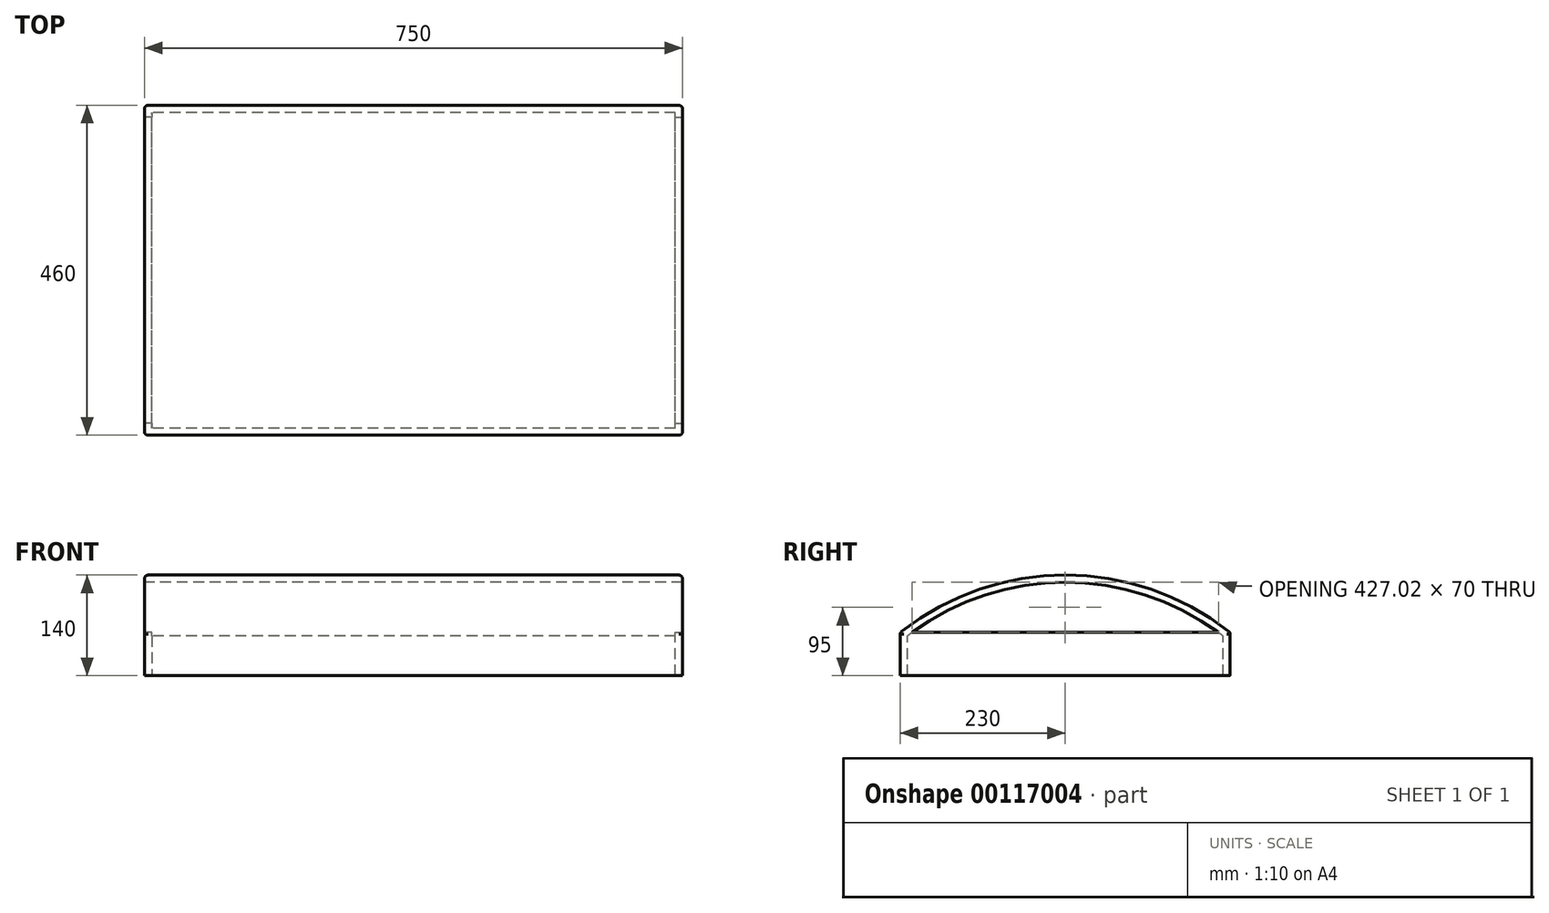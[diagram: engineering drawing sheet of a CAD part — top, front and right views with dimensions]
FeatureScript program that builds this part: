
annotation { "Feature Type Name" : "Feature", "Feature Type Description" : "" }
export const myFeature = defineFeature(function(context is Context, id is Id, definition is map)
    precondition{}
    {
        {
            var Q0;
            Q0=qCreatedBy(makeId("Right.planeOp"),FACE);
            var sketch = newSketch(context, id + "F0", { "sketchPlane" : qUnion([Q0])});
            skLineSegment(sketch, "E0.bottom", {"start": v(-230, 30) * mm, "end": v(230, 30) * mm});
            skLineSegment(sketch, "E0.top", {"start": v(-230, -30) * mm, "end": v(230, -30) * mm});
            skLineSegment(sketch, "E0.left", {"start": v(-230, 30) * mm, "end": v(-230, -30) * mm});
            skLineSegment(sketch, "E0.right", {"start": v(230, 30) * mm, "end": v(230, -30) * mm});
            skPoint(sketch, "E0.middle", {"position": v(0, 0) * mm});
            skPoint(sketch, "E1", {"position": v(0, 110) * mm});
            skFitSpline(sketch, "E2", {"points": [v(-230, 30) * mm, v(230, 30) * mm], "startDerivative": vector(460, 0) * mm, "endDerivative": vector(460, 0) * mm});
            skArc(sketch, "E3", {"start": v(230, 30) * mm, "mid": v(0, 110) * mm, "end": v(-230, 30) * mm});
            skArc(sketch, "E4.0", {"start": v(220, 25.12) * mm, "mid": v(0, 100) * mm, "end": v(-220, 25.12) * mm});
            skLineSegment(sketch, "E5.0", {"start": v(-220, 25.12) * mm, "end": v(-220, -30) * mm});
            skLineSegment(sketch, "E6.0", {"start": v(220, 25.12) * mm, "end": v(220, -30) * mm});
            skSolve(sketch);
        }
        {
            var Q0;
            {var subQ4=sQuery(id+"F0.wireOp",EDGE,"E0.left");Q0=makeQuery(id+"F0.imprint","IMPRINT",FACE,{"disambiguationData":[TD([[makeQuery(id+"F0.imprint","IMPRINT",EDGE,{"derivedFrom":subQ4}),1.0]])]});}
            var Q1;
            {var subQ0=sQuery(id+"F0.wireOp",EDGE,"E3");Q1=makeQuery(id+"F0.imprint","IMPRINT",FACE,{"disambiguationData":[TD([[makeQuery(id+"F0.imprint","IMPRINT",EDGE,{"derivedFrom":subQ0}),1.0]])]});}
            var Q2;
            {var subQ4=sQuery(id+"F0.wireOp",EDGE,"E0.right");Q2=makeQuery(id+"F0.imprint","IMPRINT",FACE,{"disambiguationData":[TD([[makeQuery(id+"F0.imprint","IMPRINT",EDGE,{"derivedFrom":subQ4}),-1.0]])]});}
            extrude(context, id + "F1", {"entities" : qUnion([Q0, Q1, Q2]), "depth" : 750 * mm});
        }
        {
            var Q0;
            {var subQ0=sQuery(id+"F0.wireOp",EDGE,"E3");Q0=makeQuery(id+"F0.imprint","IMPRINT",FACE,{"disambiguationData":[TD([[makeQuery(id+"F0.imprint","IMPRINT",EDGE,{"derivedFrom":subQ0}),1.0]])]});}
            var Q1;
            {var subQ4=sQuery(id+"F0.wireOp",EDGE,"E0.left");Q1=makeQuery(id+"F0.imprint","IMPRINT",FACE,{"disambiguationData":[TD([[makeQuery(id+"F0.imprint","IMPRINT",EDGE,{"derivedFrom":subQ4}),1.0]])]});}
            var Q2;
            {var subQ0=sQuery(id+"F0.wireOp",EDGE,"E5.0");Q2=makeQuery(id+"F0.imprint","IMPRINT",FACE,{"disambiguationData":[TD([[makeQuery(id+"F0.imprint","IMPRINT",EDGE,{"derivedFrom":subQ0}),1.0]])]});}
            var Q3;
            {var subQ0=sQuery(id+"F0.wireOp",EDGE,"E4.0");var subQ1=sQuery(id+"F0.wireOp",EDGE,"E2");var subQ2=makeQuery(id+"F0.imprint","INTERSECT",VERTEX,{"disambiguationData":[OD(0.0)],"derivedFrom":[subQ1,subQ0]});Q3=makeQuery(id+"F0.imprint","IMPRINT",FACE,{"disambiguationData":[TD([[makeQuery(id+"F0.imprint","IMPRINT",EDGE,{"disambiguationData":[TD([[subQ2,-1.0]])],"derivedFrom":subQ1}),1.0]])]});}
            var Q4;
            {var subQ4=sQuery(id+"F0.wireOp",EDGE,"E0.right");Q4=makeQuery(id+"F0.imprint","IMPRINT",FACE,{"disambiguationData":[TD([[makeQuery(id+"F0.imprint","IMPRINT",EDGE,{"derivedFrom":subQ4}),-1.0]])]});}
            extrude(context, id + "F2", {"entities" : qUnion([Q0, Q1, Q2, Q3, Q4]), "depth" : 10 * mm});
        }
        {
            var Q0;
            Q0=qCreatedBy(makeId("Right.planeOp"),FACE);
            cPlane(context, id + "F3", {"entities" : qUnion([Q0]), "cplaneType" : CPlaneType.OFFSET, "offset" : 375 * mm, "width" : 150 * mm, "height" : 150 * mm});
        }
        {
            var Q0;
            Q0=makeQuery(id+"F2.opExtrude","SWEPT_BODY",BODY,{"disambiguationData":[OSD([sQuery(id+"F0.wireOp",EDGE,"E0.top"),sQuery(id+"F0.wireOp",EDGE,"E0.left"),sQuery(id+"F0.wireOp",EDGE,"E0.right"),sQuery(id+"F0.wireOp",EDGE,"E3")])]});
            var Q1;
            Q1=qCreatedBy(id+"F3.planeOp",FACE);
            mirror(context, id + "F4", {"operationType" : NewBodyOperationType.ADD, "entities" : qUnion([Q0]), "mirrorPlane" : qUnion([Q1])});
        }
        {
            var Q0;
            Q0=makeQuery(id+"F1.opExtrude","CAP_EDGE",EDGE,{"disambiguationData":[OSD([sQuery(id+"F0.wireOp",EDGE,"E0.left")])],"isStart":true});
            var Q1;
            Q1=makeQuery(id+"F1.opExtrude","CAP_EDGE",EDGE,{"disambiguationData":[OSD([sQuery(id+"F0.wireOp",EDGE,"E0.left")])],"isStart":false});
            var Q2;
            Q2=makeQuery(id+"F1.opExtrude","CAP_EDGE",EDGE,{"disambiguationData":[OSD([sQuery(id+"F0.wireOp",EDGE,"E0.right")])],"isStart":false});
            var Q3;
            Q3=makeQuery(id+"F1.opExtrude","CAP_EDGE",EDGE,{"disambiguationData":[OSD([sQuery(id+"F0.wireOp",EDGE,"E0.right")])],"isStart":true});
            fillet(context, id + "F5", {"entities" : qUnion([Q0, Q1, Q2, Q3]), "radius" : 5 * mm, "tangentPropagation" : true, "allowEdgeOverflow" : false});
        }
        {
            var Q0;
            Q0=makeQuery(id+"F1.opExtrude","CAP_EDGE",EDGE,{"disambiguationData":[OSD([sQuery(id+"F0.wireOp",EDGE,"E3")])],"isStart":false});
            var Q1;
            Q1=makeQuery(id+"F1.opExtrude","SWEPT_EDGE",EDGE,{"disambiguationData":[OSD([sQuery(id+"F0.wireOp",EDGE,"E0.right"),sQuery(id+"F0.wireOp",EDGE,"E2"),sQuery(id+"F0.wireOp",EDGE,"E3")])]});
            var Q2;
            Q2=makeQuery(id+"F1.opExtrude","CAP_EDGE",EDGE,{"disambiguationData":[OSD([sQuery(id+"F0.wireOp",EDGE,"E3")])],"isStart":true});
            var Q3;
            Q3=makeQuery(id+"F1.opExtrude","SWEPT_EDGE",EDGE,{"disambiguationData":[OSD([sQuery(id+"F0.wireOp",EDGE,"E0.left"),sQuery(id+"F0.wireOp",EDGE,"E2"),sQuery(id+"F0.wireOp",EDGE,"E3")])]});
            fillet(context, id + "F6", {"entities" : qUnion([Q0, Q1, Q2, Q3]), "radius" : 5 * mm, "tangentPropagation" : true, "allowEdgeOverflow" : false});
        }
    });
